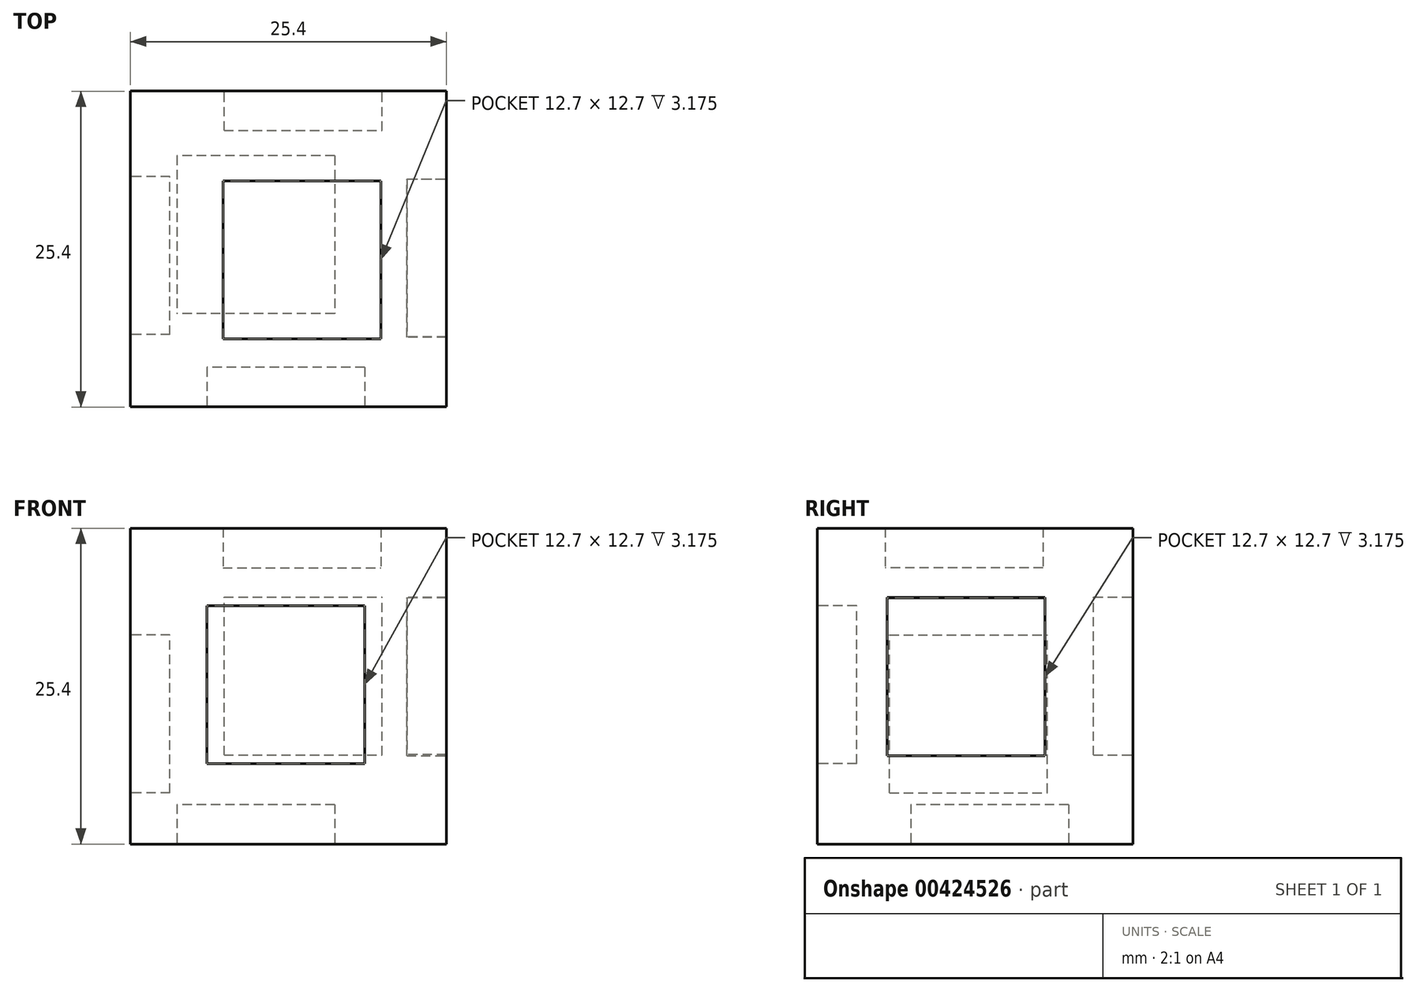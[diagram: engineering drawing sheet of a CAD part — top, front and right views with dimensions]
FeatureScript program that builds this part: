
annotation { "Feature Type Name" : "Feature", "Feature Type Description" : "" }
export const myFeature = defineFeature(function(context is Context, id is Id, definition is map)
    precondition{}
    {
        {
            var Q0;
            Q0=qCreatedBy(makeId("Top.planeOp"),FACE);
            var sketch = newSketch(context, id + "F0", { "sketchPlane" : qUnion([Q0])});
            skLineSegment(sketch, "E0.bottom", {"start": v(-14.65, 15) * mm, "end": v(10.75, 15) * mm});
            skLineSegment(sketch, "E0.top", {"start": v(-14.65, -10.4) * mm, "end": v(10.75, -10.4) * mm});
            skLineSegment(sketch, "E0.left", {"start": v(-14.65, 15) * mm, "end": v(-14.65, -10.4) * mm});
            skLineSegment(sketch, "E0.right", {"start": v(10.75, 15) * mm, "end": v(10.75, -10.4) * mm});
            skSolve(sketch);
        }
        {
            var Q0;
            Q0=makeQuery(id+"F0.imprint","IMPRINT",FACE,{"disambiguationData":[TD([[makeQuery(id+"F0.imprint","IMPRINT",EDGE,{"derivedFrom":sQuery(id+"F0.wireOp",EDGE,"E0.bottom")}),-1.0]])]});
            extrude(context, id + "F1", {"entities" : qUnion([Q0]), "depth" : 25.4 * mm});
        }
        {
            var Q0;
            Q0=makeQuery(id+"F1.opExtrude","CAP_FACE",FACE,{"disambiguationData":[OSD([sQuery(id+"F0.wireOp",EDGE,"E0.bottom"),sQuery(id+"F0.wireOp",EDGE,"E0.top"),sQuery(id+"F0.wireOp",EDGE,"E0.left"),sQuery(id+"F0.wireOp",EDGE,"E0.right")])],"isStart":false});
            var sketch = newSketch(context, id + "F2", { "sketchPlane" : qUnion([Q0])});
            skLineSegment(sketch, "E1.bottom", {"start": v(-7.21, 7.77) * mm, "end": v(5.49, 7.77) * mm});
            skLineSegment(sketch, "E1.top", {"start": v(-7.21, -4.93) * mm, "end": v(5.49, -4.93) * mm});
            skLineSegment(sketch, "E1.left", {"start": v(-7.21, 7.77) * mm, "end": v(-7.21, -4.93) * mm});
            skLineSegment(sketch, "E1.right", {"start": v(5.49, 7.77) * mm, "end": v(5.49, -4.93) * mm});
            skSolve(sketch);
        }
        {
            var Q0;
            Q0=makeQuery(id+"F2.imprint","IMPRINT",FACE,{"disambiguationData":[TD([[makeQuery(id+"F2.imprint","IMPRINT",EDGE,{"derivedFrom":sQuery(id+"F2.wireOp",EDGE,"E1.bottom")}),-1.0]])]});
            extrude(context, id + "F3", {"entities" : qUnion([Q0]), "operationType" : NewBodyOperationType.REMOVE, "oppositeDirection" : true, "depth" : 3.17 * mm});
        }
        {
            var Q0;
            Q0=makeQuery(id+"F1.opExtrude","SWEPT_FACE",FACE,{"disambiguationData":[OSD([sQuery(id+"F0.wireOp",EDGE,"E0.top")])]});
            var sketch = newSketch(context, id + "F4", { "sketchPlane" : qUnion([Q0])});
            skLineSegment(sketch, "E2.bottom", {"start": v(4.2, 6.48) * mm, "end": v(-8.5, 6.48) * mm});
            skLineSegment(sketch, "E2.top", {"start": v(4.2, 19.18) * mm, "end": v(-8.5, 19.18) * mm});
            skLineSegment(sketch, "E2.left", {"start": v(4.2, 6.48) * mm, "end": v(4.2, 19.18) * mm});
            skLineSegment(sketch, "E2.right", {"start": v(-8.5, 6.48) * mm, "end": v(-8.5, 19.18) * mm});
            skSolve(sketch);
        }
        {
            var Q0;
            Q0=makeQuery(id+"F4.imprint","IMPRINT",FACE,{"disambiguationData":[TD([[makeQuery(id+"F4.imprint","IMPRINT",EDGE,{"derivedFrom":sQuery(id+"F4.wireOp",EDGE,"E2.bottom")}),-1.0]])]});
            extrude(context, id + "F5", {"entities" : qUnion([Q0]), "operationType" : NewBodyOperationType.REMOVE, "oppositeDirection" : true, "depth" : 3.17 * mm});
        }
        {
            var Q0;
            Q0=makeQuery(id+"F1.opExtrude","SWEPT_FACE",FACE,{"disambiguationData":[OSD([sQuery(id+"F0.wireOp",EDGE,"E0.left")])]});
            var sketch = newSketch(context, id + "F6", { "sketchPlane" : qUnion([Q0])});
            skLineSegment(sketch, "E3.bottom", {"start": v(-267.6, 5.78) * mm, "end": v(-280.3, 5.78) * mm});
            skLineSegment(sketch, "E3.top", {"start": v(-267.6, 18.48) * mm, "end": v(-280.3, 18.48) * mm});
            skLineSegment(sketch, "E3.left", {"start": v(-267.6, 5.78) * mm, "end": v(-267.6, 18.48) * mm});
            skLineSegment(sketch, "E3.right", {"start": v(-280.3, 5.78) * mm, "end": v(-280.3, 18.48) * mm});
            skLineSegment(sketch, "E4.bottom", {"start": v(4.58, 4.13) * mm, "end": v(-8.12, 4.13) * mm});
            skLineSegment(sketch, "E4.top", {"start": v(4.58, 16.83) * mm, "end": v(-8.12, 16.83) * mm});
            skLineSegment(sketch, "E4.left", {"start": v(4.58, 4.13) * mm, "end": v(4.58, 16.83) * mm});
            skLineSegment(sketch, "E4.right", {"start": v(-8.12, 4.13) * mm, "end": v(-8.12, 16.83) * mm});
            skSolve(sketch);
        }
        {
            var Q0;
            Q0=makeQuery(id+"F6.imprint","IMPRINT",FACE,{"disambiguationData":[TD([[makeQuery(id+"F6.imprint","IMPRINT",EDGE,{"derivedFrom":sQuery(id+"F6.wireOp",EDGE,"E4.bottom")}),-1.0]])]});
            extrude(context, id + "F7", {"entities" : qUnion([Q0]), "operationType" : NewBodyOperationType.REMOVE, "oppositeDirection" : true, "depth" : 3.17 * mm});
        }
        {
            var Q0;
            Q0=makeQuery(id+"F1.opExtrude","SWEPT_FACE",FACE,{"disambiguationData":[OSD([sQuery(id+"F0.wireOp",EDGE,"E0.right")])]});
            var sketch = newSketch(context, id + "F8", { "sketchPlane" : qUnion([Q0])});
            skLineSegment(sketch, "E5.bottom", {"start": v(7.93, 7.11) * mm, "end": v(-4.77, 7.11) * mm});
            skLineSegment(sketch, "E5.top", {"start": v(7.93, 19.81) * mm, "end": v(-4.77, 19.81) * mm});
            skLineSegment(sketch, "E5.left", {"start": v(7.93, 7.11) * mm, "end": v(7.93, 19.81) * mm});
            skLineSegment(sketch, "E5.right", {"start": v(-4.77, 7.11) * mm, "end": v(-4.77, 19.81) * mm});
            skSolve(sketch);
        }
        {
            var Q0;
            Q0=makeQuery(id+"F8.imprint","IMPRINT",FACE,{"disambiguationData":[TD([[makeQuery(id+"F8.imprint","IMPRINT",EDGE,{"derivedFrom":sQuery(id+"F8.wireOp",EDGE,"E5.bottom")}),-1.0]])]});
            extrude(context, id + "F9", {"entities" : qUnion([Q0]), "operationType" : NewBodyOperationType.REMOVE, "oppositeDirection" : true, "depth" : 3.17 * mm});
        }
        {
            var Q0;
            Q0=makeQuery(id+"F1.opExtrude","CAP_FACE",FACE,{"disambiguationData":[OSD([sQuery(id+"F0.wireOp",EDGE,"E0.bottom"),sQuery(id+"F0.wireOp",EDGE,"E0.top"),sQuery(id+"F0.wireOp",EDGE,"E0.left"),sQuery(id+"F0.wireOp",EDGE,"E0.right")])],"isStart":true});
            var sketch = newSketch(context, id + "F10", { "sketchPlane" : qUnion([Q0])});
            skLineSegment(sketch, "E6.bottom", {"start": v(1.77, -9.81) * mm, "end": v(-10.93, -9.81) * mm});
            skLineSegment(sketch, "E6.top", {"start": v(1.77, 2.89) * mm, "end": v(-10.93, 2.89) * mm});
            skLineSegment(sketch, "E6.left", {"start": v(1.77, -9.81) * mm, "end": v(1.77, 2.89) * mm});
            skLineSegment(sketch, "E6.right", {"start": v(-10.93, -9.81) * mm, "end": v(-10.93, 2.89) * mm});
            skSolve(sketch);
        }
        {
            var Q0;
            Q0=makeQuery(id+"F10.imprint","IMPRINT",FACE,{"disambiguationData":[TD([[makeQuery(id+"F10.imprint","IMPRINT",EDGE,{"derivedFrom":sQuery(id+"F10.wireOp",EDGE,"E6.bottom")}),-1.0]])]});
            extrude(context, id + "F11", {"entities" : qUnion([Q0]), "operationType" : NewBodyOperationType.REMOVE, "oppositeDirection" : true, "depth" : 3.17 * mm});
        }
        {
            var Q0;
            Q0=makeQuery(id+"F1.opExtrude","SWEPT_FACE",FACE,{"disambiguationData":[OSD([sQuery(id+"F0.wireOp",EDGE,"E0.bottom")])]});
            var sketch = newSketch(context, id + "F12", { "sketchPlane" : qUnion([Q0])});
            skLineSegment(sketch, "E7.bottom", {"start": v(7.12, 7.15) * mm, "end": v(-5.58, 7.15) * mm});
            skLineSegment(sketch, "E7.top", {"start": v(7.12, 19.85) * mm, "end": v(-5.58, 19.85) * mm});
            skLineSegment(sketch, "E7.left", {"start": v(7.12, 7.15) * mm, "end": v(7.12, 19.85) * mm});
            skLineSegment(sketch, "E7.right", {"start": v(-5.58, 7.15) * mm, "end": v(-5.58, 19.85) * mm});
            skSolve(sketch);
        }
        {
            var Q0;
            Q0=makeQuery(id+"F12.imprint","IMPRINT",FACE,{"disambiguationData":[TD([[makeQuery(id+"F12.imprint","IMPRINT",EDGE,{"derivedFrom":sQuery(id+"F12.wireOp",EDGE,"E7.bottom")}),-1.0]])]});
            var Q1;
            Q1=sQuery(id+"F12.wireOp",EDGE,"E7.top");
            var Q2;
            Q2=sQuery(id+"F12.wireOp",EDGE,"E7.left");
            var Q3;
            Q3=sQuery(id+"F12.wireOp",EDGE,"E7.right");
            var Q4;
            Q4=sQuery(id+"F12.wireOp",EDGE,"E7.bottom");
            extrude(context, id + "F13", {"entities" : qUnion([Q0]), "operationType" : NewBodyOperationType.REMOVE, "surfaceEntities" : qUnion([Q1, Q2, Q3, Q4]), "oppositeDirection" : true, "depth" : 3.17 * mm});
        }
        {
            var Q0;
            Q0=makeQuery(id+"F9.boolean.opBoolean","COPY",FACE,{"derivedFrom":makeQuery(id+"F9.opExtrude","CAP_FACE",FACE,{"disambiguationData":[OSD([sQuery(id+"F8.wireOp",EDGE,"E5.bottom"),sQuery(id+"F8.wireOp",EDGE,"E5.top"),sQuery(id+"F8.wireOp",EDGE,"E5.left"),sQuery(id+"F8.wireOp",EDGE,"E5.right")])],"isStart":false})});
            var sketch = newSketch(context, id + "F14", { "sketchPlane" : qUnion([Q0])});
            skLineSegment(sketch, "E8.bottom", {"start": v(-4.78, 19.84) * mm, "end": v(7.92, 19.84) * mm});
            skLineSegment(sketch, "E8.top", {"start": v(-4.78, 7.2) * mm, "end": v(7.92, 7.2) * mm});
            skLineSegment(sketch, "E8.left", {"start": v(-4.78, 19.84) * mm, "end": v(-4.78, 7.2) * mm});
            skLineSegment(sketch, "E8.right", {"start": v(7.92, 19.84) * mm, "end": v(7.92, 7.2) * mm});
            skSolve(sketch);
        }
        {
            var Q0;
            {var subQ1=sQuery(id+"F14.wireOp",EDGE,"E8.bottom");Q0=makeQuery(id+"F14.imprint","IMPRINT",FACE,{"disambiguationData":[TD([[makeQuery(id+"F14.imprint","IMPRINT",EDGE,{"derivedFrom":subQ1}),-1.0]])]});}
            extrude(context, id + "F15", {"entities" : qUnion([Q0]), "depth" : 3.17 * mm});
        }
        {
            var Q0;
            Q0=makeQuery(id+"F3.boolean.opBoolean","COPY",FACE,{"derivedFrom":makeQuery(id+"F3.opExtrude","CAP_FACE",FACE,{"disambiguationData":[OSD([sQuery(id+"F2.wireOp",EDGE,"E1.bottom"),sQuery(id+"F2.wireOp",EDGE,"E1.top"),sQuery(id+"F2.wireOp",EDGE,"E1.left"),sQuery(id+"F2.wireOp",EDGE,"E1.right")])],"isStart":false})});
            var sketch = newSketch(context, id + "F16", { "sketchPlane" : qUnion([Q0])});
            skLineSegment(sketch, "E9.bottom", {"start": v(-7.21, 7.77) * mm, "end": v(5.49, 7.77) * mm});
            skLineSegment(sketch, "E9.top", {"start": v(-7.21, -4.93) * mm, "end": v(5.49, -4.93) * mm});
            skLineSegment(sketch, "E9.left", {"start": v(-7.21, 7.77) * mm, "end": v(-7.21, -4.93) * mm});
            skLineSegment(sketch, "E9.right", {"start": v(5.49, 7.77) * mm, "end": v(5.49, -4.93) * mm});
            skSolve(sketch);
        }
        {
            var Q0;
            Q0 = qSketchRegion(id + "F16", true);
            extrude(context, id + "F17", {"entities" : qUnion([Q0]), "depth" : 3.17 * mm});
        }
        {
            var Q0;
            Q0=makeQuery(id+"F9.boolean.opBoolean","COPY",FACE,{"derivedFrom":makeQuery(id+"F9.opExtrude","CAP_FACE",FACE,{"disambiguationData":[OSD([sQuery(id+"F8.wireOp",EDGE,"E5.bottom"),sQuery(id+"F8.wireOp",EDGE,"E5.top"),sQuery(id+"F8.wireOp",EDGE,"E5.left"),sQuery(id+"F8.wireOp",EDGE,"E5.right")])],"isStart":false})});
            var sketch = newSketch(context, id + "F18", { "sketchPlane" : qUnion([Q0])});
            skLineSegment(sketch, "E10.bottom", {"start": v(7.93, 19.81) * mm, "end": v(-4.77, 19.81) * mm});
            skLineSegment(sketch, "E10.top", {"start": v(7.93, 7.11) * mm, "end": v(-4.77, 7.11) * mm});
            skLineSegment(sketch, "E10.left", {"start": v(7.93, 19.81) * mm, "end": v(7.93, 7.11) * mm});
            skLineSegment(sketch, "E10.right", {"start": v(-4.77, 19.81) * mm, "end": v(-4.77, 7.11) * mm});
            skSolve(sketch);
        }
        {
            var Q0;
            Q0 = qSketchRegion(id + "F18", true);
            extrude(context, id + "F19", {"entities" : qUnion([Q0]), "depth" : 3.17 * mm});
        }
        {
            var Q0;
            Q0=makeQuery(id+"F5.boolean.opBoolean","COPY",FACE,{"derivedFrom":makeQuery(id+"F5.opExtrude","CAP_FACE",FACE,{"disambiguationData":[OSD([sQuery(id+"F4.wireOp",EDGE,"E2.bottom"),sQuery(id+"F4.wireOp",EDGE,"E2.top"),sQuery(id+"F4.wireOp",EDGE,"E2.left"),sQuery(id+"F4.wireOp",EDGE,"E2.right")])],"isStart":false})});
            var sketch = newSketch(context, id + "F20", { "sketchPlane" : qUnion([Q0])});
            skLineSegment(sketch, "E11.bottom", {"start": v(4.2, 19.18) * mm, "end": v(-8.5, 19.18) * mm});
            skLineSegment(sketch, "E11.top", {"start": v(4.2, 6.48) * mm, "end": v(-8.5, 6.48) * mm});
            skLineSegment(sketch, "E11.left", {"start": v(4.2, 19.18) * mm, "end": v(4.2, 6.48) * mm});
            skLineSegment(sketch, "E11.right", {"start": v(-8.5, 19.18) * mm, "end": v(-8.5, 6.48) * mm});
            skSolve(sketch);
        }
        {
            var Q0;
            Q0 = qSketchRegion(id + "F20", true);
            extrude(context, id + "F21", {"entities" : qUnion([Q0]), "depth" : 3.17 * mm});
        }
        {
            var Q0;
            Q0=makeQuery(id+"F7.boolean.opBoolean","COPY",FACE,{"derivedFrom":makeQuery(id+"F7.opExtrude","CAP_FACE",FACE,{"disambiguationData":[OSD([sQuery(id+"F6.wireOp",EDGE,"E4.bottom"),sQuery(id+"F6.wireOp",EDGE,"E4.top"),sQuery(id+"F6.wireOp",EDGE,"E4.left"),sQuery(id+"F6.wireOp",EDGE,"E4.right")])],"isStart":false})});
            var sketch = newSketch(context, id + "F22", { "sketchPlane" : qUnion([Q0])});
            skLineSegment(sketch, "E12.bottom", {"start": v(4.58, 16.83) * mm, "end": v(-8.12, 16.83) * mm});
            skLineSegment(sketch, "E12.top", {"start": v(4.58, 4.13) * mm, "end": v(-8.12, 4.13) * mm});
            skLineSegment(sketch, "E12.left", {"start": v(4.58, 16.83) * mm, "end": v(4.58, 4.13) * mm});
            skLineSegment(sketch, "E12.right", {"start": v(-8.12, 16.83) * mm, "end": v(-8.12, 4.13) * mm});
            skSolve(sketch);
        }
        {
            var Q0;
            Q0=makeQuery(id+"F22.imprint","IMPRINT",FACE,{"disambiguationData":[TD([[makeQuery(id+"F22.imprint","IMPRINT",EDGE,{"derivedFrom":sQuery(id+"F22.wireOp",EDGE,"E12.bottom")}),1.0]])]});
            extrude(context, id + "F23", {"entities" : qUnion([Q0]), "depth" : 3.17 * mm});
        }
        {
            var Q0;
            Q0=makeQuery(id+"F13.boolean.opBoolean","COPY",FACE,{"derivedFrom":makeQuery(id+"F13.opExtrude","CAP_FACE",FACE,{"disambiguationData":[OSD([sQuery(id+"F12.wireOp",EDGE,"E7.bottom"),sQuery(id+"F12.wireOp",EDGE,"E7.top"),sQuery(id+"F12.wireOp",EDGE,"E7.left"),sQuery(id+"F12.wireOp",EDGE,"E7.right")])],"isStart":false})});
            var sketch = newSketch(context, id + "F24", { "sketchPlane" : qUnion([Q0])});
            skLineSegment(sketch, "E13.bottom", {"start": v(7.12, 19.85) * mm, "end": v(-5.58, 19.85) * mm});
            skLineSegment(sketch, "E13.top", {"start": v(7.12, 7.15) * mm, "end": v(-5.58, 7.15) * mm});
            skLineSegment(sketch, "E13.left", {"start": v(7.12, 19.85) * mm, "end": v(7.12, 7.15) * mm});
            skLineSegment(sketch, "E13.right", {"start": v(-5.58, 19.85) * mm, "end": v(-5.58, 7.15) * mm});
            skSolve(sketch);
        }
        {
            var Q0;
            Q0=makeQuery(id+"F24.imprint","IMPRINT",FACE,{"disambiguationData":[TD([[makeQuery(id+"F24.imprint","IMPRINT",EDGE,{"derivedFrom":sQuery(id+"F24.wireOp",EDGE,"E13.bottom")}),1.0]])]});
            extrude(context, id + "F25", {"entities" : qUnion([Q0]), "depth" : 3.17 * mm});
        }
        {
            var Q0;
            Q0=makeQuery(id+"F11.boolean.opBoolean","COPY",FACE,{"derivedFrom":makeQuery(id+"F11.opExtrude","CAP_FACE",FACE,{"disambiguationData":[OSD([sQuery(id+"F10.wireOp",EDGE,"E6.bottom"),sQuery(id+"F10.wireOp",EDGE,"E6.top"),sQuery(id+"F10.wireOp",EDGE,"E6.left"),sQuery(id+"F10.wireOp",EDGE,"E6.right")])],"isStart":false})});
            var sketch = newSketch(context, id + "F26", { "sketchPlane" : qUnion([Q0])});
            skLineSegment(sketch, "E14.bottom", {"start": v(1.77, -9.81) * mm, "end": v(-10.93, -9.81) * mm});
            skLineSegment(sketch, "E14.top", {"start": v(1.77, 2.89) * mm, "end": v(-10.93, 2.89) * mm});
            skLineSegment(sketch, "E14.left", {"start": v(1.77, -9.81) * mm, "end": v(1.77, 2.89) * mm});
            skLineSegment(sketch, "E14.right", {"start": v(-10.93, -9.81) * mm, "end": v(-10.93, 2.89) * mm});
            skSolve(sketch);
        }
        {
            var Q0;
            Q0 = qSketchRegion(id + "F26", true);
            extrude(context, id + "F27", {"entities" : qUnion([Q0]), "depth" : 3.17 * mm});
        }
    });
